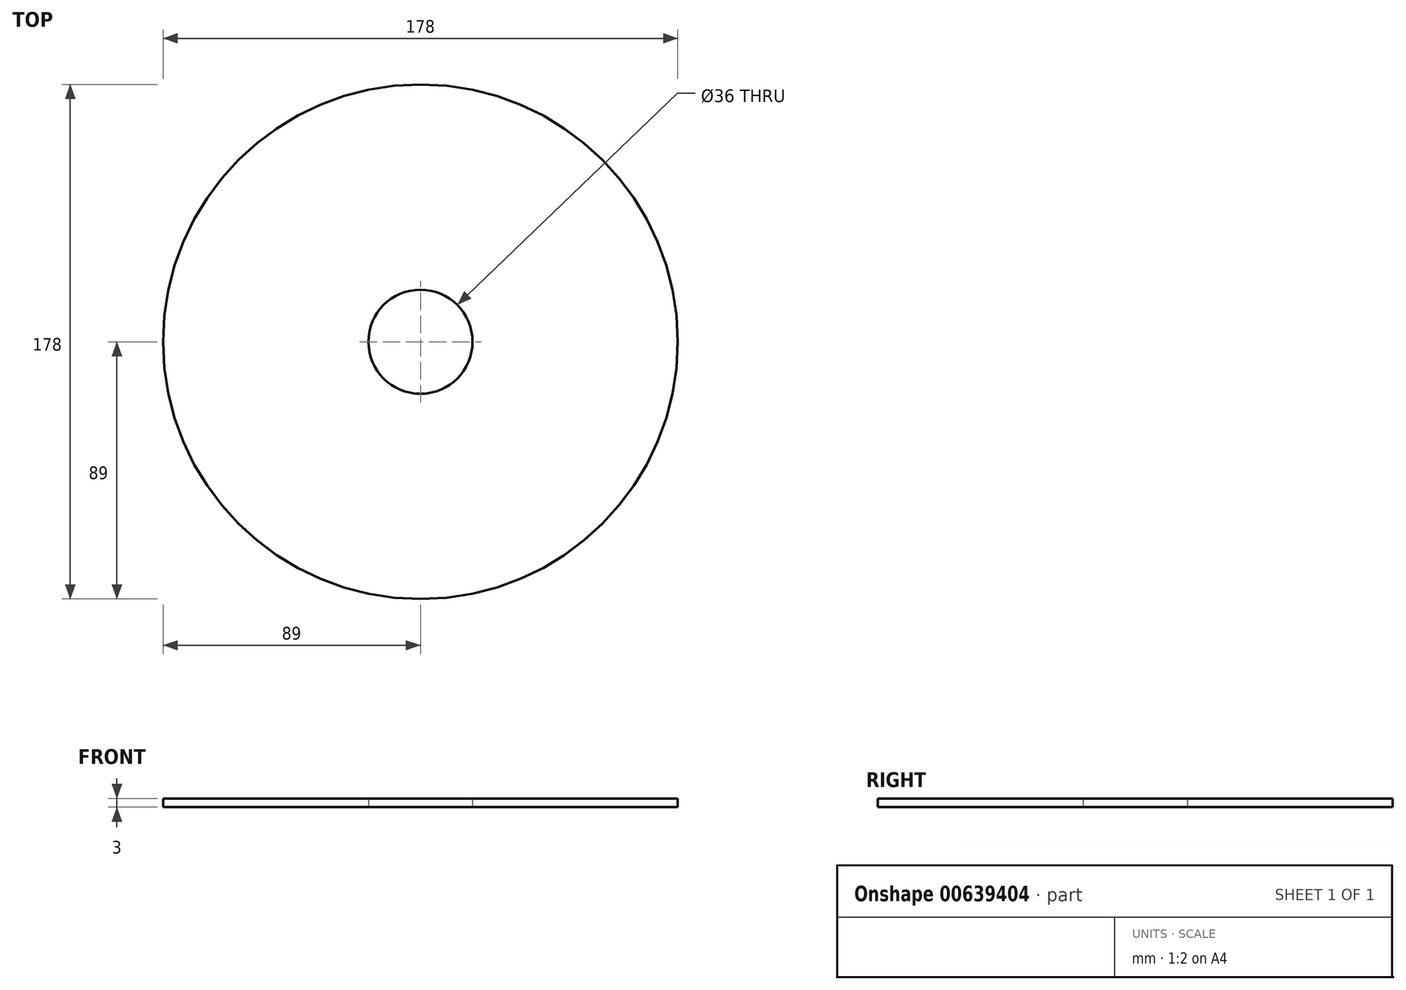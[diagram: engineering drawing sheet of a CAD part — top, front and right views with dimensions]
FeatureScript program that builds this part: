
annotation { "Feature Type Name" : "Feature", "Feature Type Description" : "" }
export const myFeature = defineFeature(function(context is Context, id is Id, definition is map)
    precondition{}
    {
        {
            var Q0;
            Q0=qCreatedBy(makeId("Top.planeOp"),FACE);
            var sketch = newSketch(context, id + "F0", { "sketchPlane" : qUnion([Q0])});
            skCircle(sketch, "E0", {"center": v(0, 0) * mm, "radius": 89 * mm});
            skCircle(sketch, "E1", {"center": v(0, 0) * mm, "radius": 18 * mm});
            skSolve(sketch);
        }
        {
            var Q0;
            Q0=makeQuery(id+"F0.imprint","IMPRINT",FACE,{"disambiguationData":[TD([[makeQuery(id+"F0.imprint","IMPRINT",EDGE,{"derivedFrom":sQuery(id+"F0.wireOp",EDGE,"E0")}),1.0]])]});
            extrude(context, id + "F1", {"entities" : qUnion([Q0]), "depth" : 3 * mm, "offsetDistance" : 25 * mm});
        }
    });
